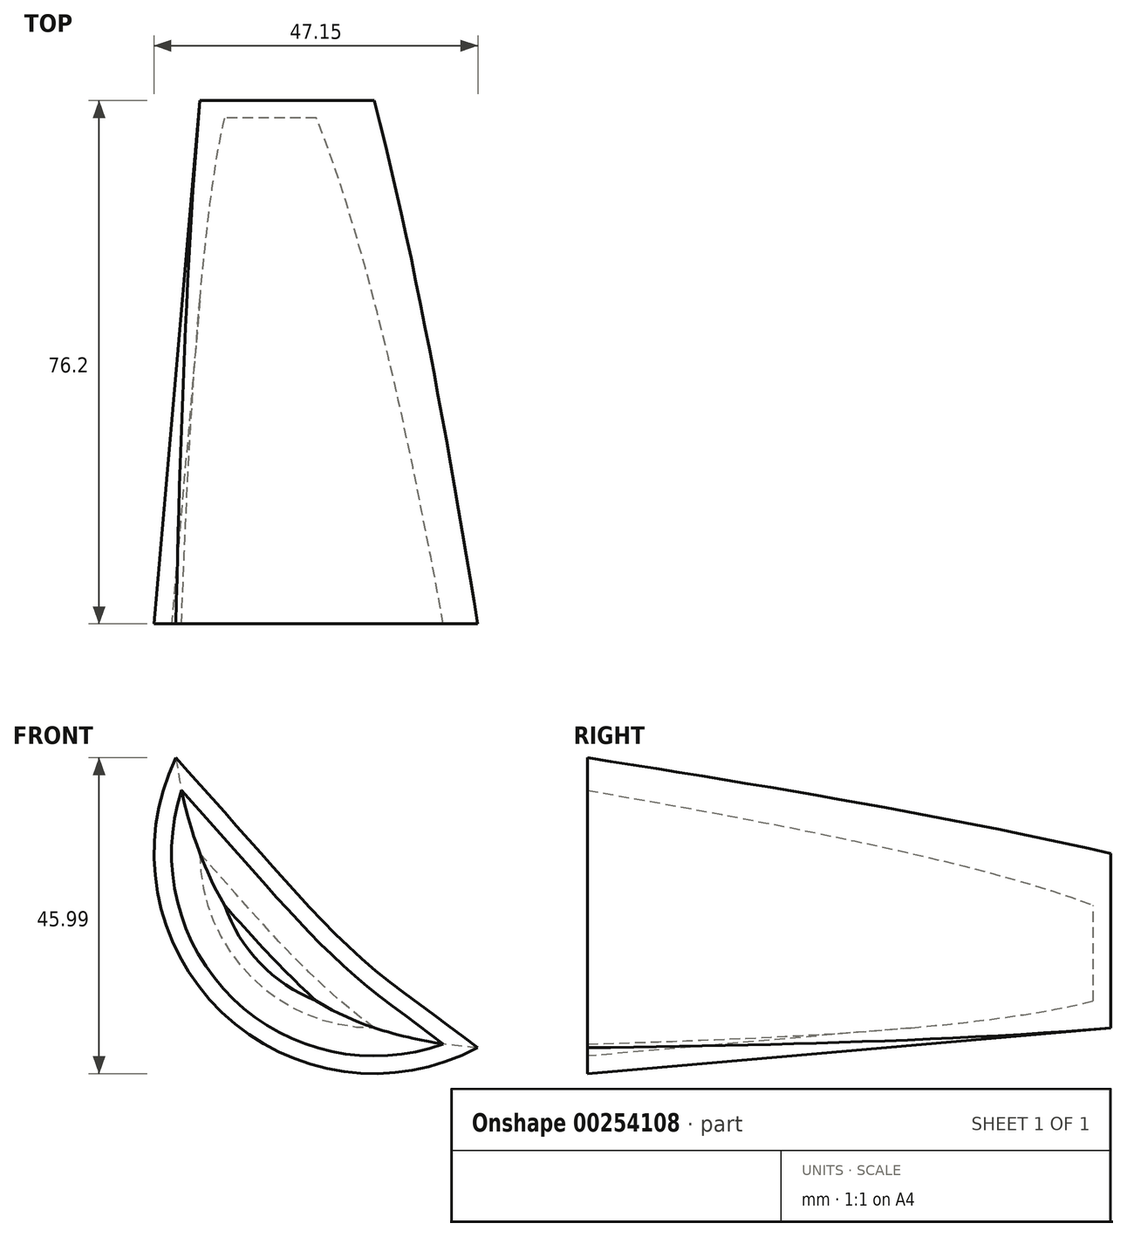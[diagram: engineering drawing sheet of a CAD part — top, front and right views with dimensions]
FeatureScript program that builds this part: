
annotation { "Feature Type Name" : "Feature", "Feature Type Description" : "" }
export const myFeature = defineFeature(function(context is Context, id is Id, definition is map)
    precondition{}
    {
        {
            var Q0;
            Q0=qCreatedBy(makeId("Front.planeOp"),FACE);
            var sketch = newSketch(context, id + "F0", { "sketchPlane" : qUnion([Q0])});
            skPoint(sketch, "E0.visualSharp", {"position": v(-53.64, 57.57) * mm});
            skPoint(sketch, "E1.visualSharp", {"position": v(-53.64, -44.03) * mm});
            skArc(sketch, "E1.filletArc", {"start": v(-53.64, -18.63) * mm, "mid": v(-46.2, -36.6) * mm, "end": v(-28.24, -44.03) * mm});
            skPoint(sketch, "E2.visualSharp", {"position": v(98.76, 57.57) * mm});
            skArc(sketch, "E2.filletArc", {"start": v(98.76, 32.17) * mm, "mid": v(91.32, 50.13) * mm, "end": v(73.36, 57.57) * mm});
            skPoint(sketch, "E3.visualSharp", {"position": v(98.76, -44.03) * mm});
            skFitSpline(sketch, "E4", {"points": [v(98.76, 32.17) * mm, v(125.69, 12.39) * mm, v(106.1, -15.04) * mm, v(98.76, -18.63) * mm, v(82.6, -25.11) * mm, v(73.36, -44.03) * mm, v(19.07, -61.21) * mm, v(-28.24, -44.03) * mm, v(-53.64, -18.63) * mm, v(-75.52, 15.75) * mm, v(-53.64, 32.17) * mm, v(-28.24, 57.57) * mm, v(-15.92, 74.23) * mm, v(4.23, 71.16) * mm, v(41.17, 73.68) * mm, v(73.36, 57.57) * mm, v(81.47, 39.81) * mm, v(98.76, 32.17) * mm]});
            skSolve(sketch);
        }
        {
            var Q0;
            Q0=makeQuery(id+"F0.imprint","IMPRINT",FACE,{"disambiguationData":[TD([[makeQuery(id+"F0.imprint","IMPRINT",EDGE,{"derivedFrom":sQuery(id+"F0.wireOp",EDGE,"E1.filletArc")}),1.0]])]});
            extrude(context, id + "F1", {"entities" : qUnion([Q0]), "depth" : 76.2 * mm, "hasDraft" : true, "draftAngle" : 5 * degree});
        }
        {
            var Q0;
            Q0=makeQuery(id+"F1.opExtrude","CAP_FACE",FACE,{"disambiguationData":[OSD([sQuery(id+"F0.wireOp",EDGE,"E1.filletArc"),sQuery(id+"F0.wireOp",EDGE,"E2.filletArc"),sQuery(id+"F0.wireOp",EDGE,"E4"),sQuery(id+"F0.wireOp",EDGE,"E4")])],"isStart":false});
            shell(context, id + "F2", {"entities" : qUnion([Q0]), "thickness" : 2.54 * mm});
        }
    });
